# Revit family: SIRELLA SLR
name_source: partatom
category: Equipement de génie climatique
revit_build: Autodesk Revit 2018 (Build: 20170223_1515(x64)
units: mm (PartAtom-declared; Revit-internal decimal feet)

## family parameters
Basée sur le plan de construction = Non
Classification = Aucun
Cote de connecteur circulaire = Utiliser le diamètre
Couper avec des vides une fois chargée = Non
Partagée = Non
Point de calcul de pièce = Non
Toujours verticalement = Oui
Type d'élément = Normal

## types (3) — shared parameters
ANGLE_CHANFREIN = 45.00°
BRANCHEMENT_TERRE = Oui
COS_PHI = 0.9
DESCR_ALIM_X = Puissance electrique, 4G2.5mm²
HAUT_MAINTENANCE = 300 mm
LARG_ENTRAXE_FIX = 300 mm
NBR_POLES = 3
NEUTRE = Non
OFFSET_MAINTENANCE = 200 mm
RAY_FIX = 25 mm  [stored 0.082021 ft]
TENSION_ALIM = 400 V

## per-type parameters (varying)
- SL300.R: DEBIT_ASPI_VIDE=300.0 m³/h; DEBIT_REFOUL_VIDE=300.0 m³/h; DESCR_ASPI=Aspiration vide ; 260 m3/h ; G 2" FEM; DESCR_REFOUL=Refoulement vide ; 260 m3/h ; G 2" FEM; DIAM_ASPI_VIDE=50 mm  [stored 0.164042 ft]; DIAM_MOT=220 mm; DIAM_REFOUL_VIDE=50 mm  [stored 0.164042 ft]; HAUTEUR=568 mm; HAUT_BOITE=166 mm; HAUT_BRIDE=35 mm; HAUT_FIX=24 mm; HAUT_OFFSET_CABLE_ELECT=36 mm; HAUT_OFFSET_REFOUL=64 mm  [stored 0.209974 ft]; HAUT_RAINURE=30 mm  [stored 0.0984252 ft]; HAUT_SILENCIEUX=195 mm; LARGEUR=472 mm; LARG_BOITE=120 mm; LARG_CHANFREIN=100 mm  [stored 0.328084 ft]; LARG_OFFSET_FIX=86 mm  [stored 0.282152 ft]; LARG_OFFSET_REFOUL=418 mm; LONGUEUR=890 mm; LONG_BOITE=120 mm; LONG_CORPS=802 mm; LONG_ENTRAXE_FIX=670 mm; LONG_MOT=339 mm; LONG_OFFSET_BOITE=192 mm; LONG_OFFSET_BRIDE_ASPI=130 mm; LONG_OFFSET_CABLE_ELECT=80 mm  [stored 0.262467 ft]; LONG_OFFSET_FIX=67 mm; LONG_REFOUL=26 mm; NIVEAU_SONORE=70; POIDS=300 mm; POIDS(Kg)=300 mm; PUISSANCE_APPARENTE=6111 VA; PUISS_ELECT=6 kW; RAY_BRIDE=25 mm  [stored 0.082021 ft]; RAY_CABLE_ELECT=5 mm  [stored 0.0164042 ft]; RAY_MOT=110 mm  [stored 0.360892 ft]; SORTIE_CABLE_ELECT=-60 mm
- SL150.R: DEBIT_ASPI_VIDE=150.0 m³/h; DEBIT_REFOUL_VIDE=150.0 m³/h; DESCR_ASPI=Aspiration vide ; 140 m3/h ; G 1_1/2" FEM; DESCR_REFOUL=Refoulement vide ; 140 m3/h ; G 1_1/2" FEM; DIAM_ASPI_VIDE=40 mm  [stored 0.131234 ft]; DIAM_MOT=191 mm; DIAM_REFOUL_VIDE=40 mm  [stored 0.131234 ft]; HAUTEUR=505 mm; HAUT_BOITE=142 mm  [stored 0.465879 ft]; HAUT_BRIDE=38 mm  [stored 0.124672 ft]; HAUT_FIX=15 mm  [stored 0.0492126 ft]; HAUT_OFFSET_CABLE_ELECT=32 mm  [stored 0.104987 ft]; HAUT_OFFSET_REFOUL=49 mm  [stored 0.160761 ft]; HAUT_RAINURE=20 mm  [stored 0.0656168 ft]; HAUT_SILENCIEUX=168 mm; LARGEUR=430 mm; LARG_BOITE=104 mm; LARG_CHANFREIN=80 mm  [stored 0.262467 ft]; LARG_OFFSET_FIX=65 mm  [stored 0.213255 ft]; LARG_OFFSET_REFOUL=370 mm; LONGUEUR=774 mm; LONG_BOITE=87 mm  [stored 0.285433 ft]; LONG_CORPS=730 mm; LONG_ENTRAXE_FIX=600 mm; LONG_MOT=291 mm; LONG_OFFSET_BOITE=178 mm; LONG_OFFSET_BRIDE_ASPI=134 mm; LONG_OFFSET_CABLE_ELECT=59 mm; LONG_OFFSET_FIX=65 mm  [stored 0.213255 ft]; LONG_REFOUL=14 mm  [stored 0.0459318 ft]; NIVEAU_SONORE=69; POIDS=180 mm; POIDS(Kg)=180 mm; PUISSANCE_APPARENTE=3333 VA; PUISS_ELECT=3 kW; RAY_BRIDE=20 mm  [stored 0.0656168 ft]; RAY_CABLE_ELECT=1 mm  [stored 0.00328084 ft]; RAY_MOT=95 mm; SORTIE_CABLE_ELECT=-74 mm
- SL100.R: Code d'assemblage=824410; DEBIT_ASPI_VIDE=150.0 m³/h; DEBIT_REFOUL_VIDE=150.0 m³/h; DESCR_ASPI=Aspiration vide ; 90 m3/h ; G 1_1/2" FEM; DESCR_REFOUL=Refoulement vide ; 90 m3/h ; G 1_1/2" FEM; DIAM_ASPI_VIDE=40 mm  [stored 0.131234 ft]; DIAM_MOT=172 mm; DIAM_REFOUL_VIDE=40 mm  [stored 0.131234 ft]; Description=VACUUM PUMP 100m3/h; Fabricant=MIL'S; HAUTEUR=505 mm; HAUT_BOITE=137 mm; HAUT_BRIDE=37 mm; HAUT_FIX=15 mm  [stored 0.0492126 ft]; HAUT_OFFSET_CABLE_ELECT=34 mm; HAUT_OFFSET_REFOUL=49 mm  [stored 0.160761 ft]; HAUT_RAINURE=20 mm  [stored 0.0656168 ft]; HAUT_SILENCIEUX=168 mm; LARGEUR=430 mm; LARG_BOITE=103 mm  [stored 0.337927 ft]; LARG_CHANFREIN=80 mm  [stored 0.262467 ft]; LARG_OFFSET_FIX=65 mm  [stored 0.213255 ft]; LARG_OFFSET_REFOUL=370 mm; LONGUEUR=780 mm; LONG_BOITE=87 mm  [stored 0.285433 ft]; LONG_CORPS=730 mm; LONG_ENTRAXE_FIX=600 mm; LONG_MOT=297 mm; LONG_OFFSET_BOITE=165 mm; LONG_OFFSET_BRIDE_ASPI=134 mm; LONG_OFFSET_CABLE_ELECT=59 mm; LONG_OFFSET_FIX=65 mm  [stored 0.213255 ft]; LONG_REFOUL=14 mm  [stored 0.0459318 ft]; Lien espace client=https://www.mils.fr; Modèle=SIRELLA SL100.R; NIVEAU_SONORE=69; POIDS=170 mm; POIDS(Kg)=170 mm; PUISSANCE_APPARENTE=2444 VA; PUISS_ELECT=2 kW; RAY_BRIDE=20 mm  [stored 0.0656168 ft]; RAY_CABLE_ELECT=5 mm  [stored 0.0164042 ft]; RAY_MOT=86 mm  [stored 0.282152 ft]; SORTIE_CABLE_ELECT=-74 mm

note: [stored X ft] marks values corroborated as IEEE doubles in the binary element streams (Revit-internal decimal feet)
